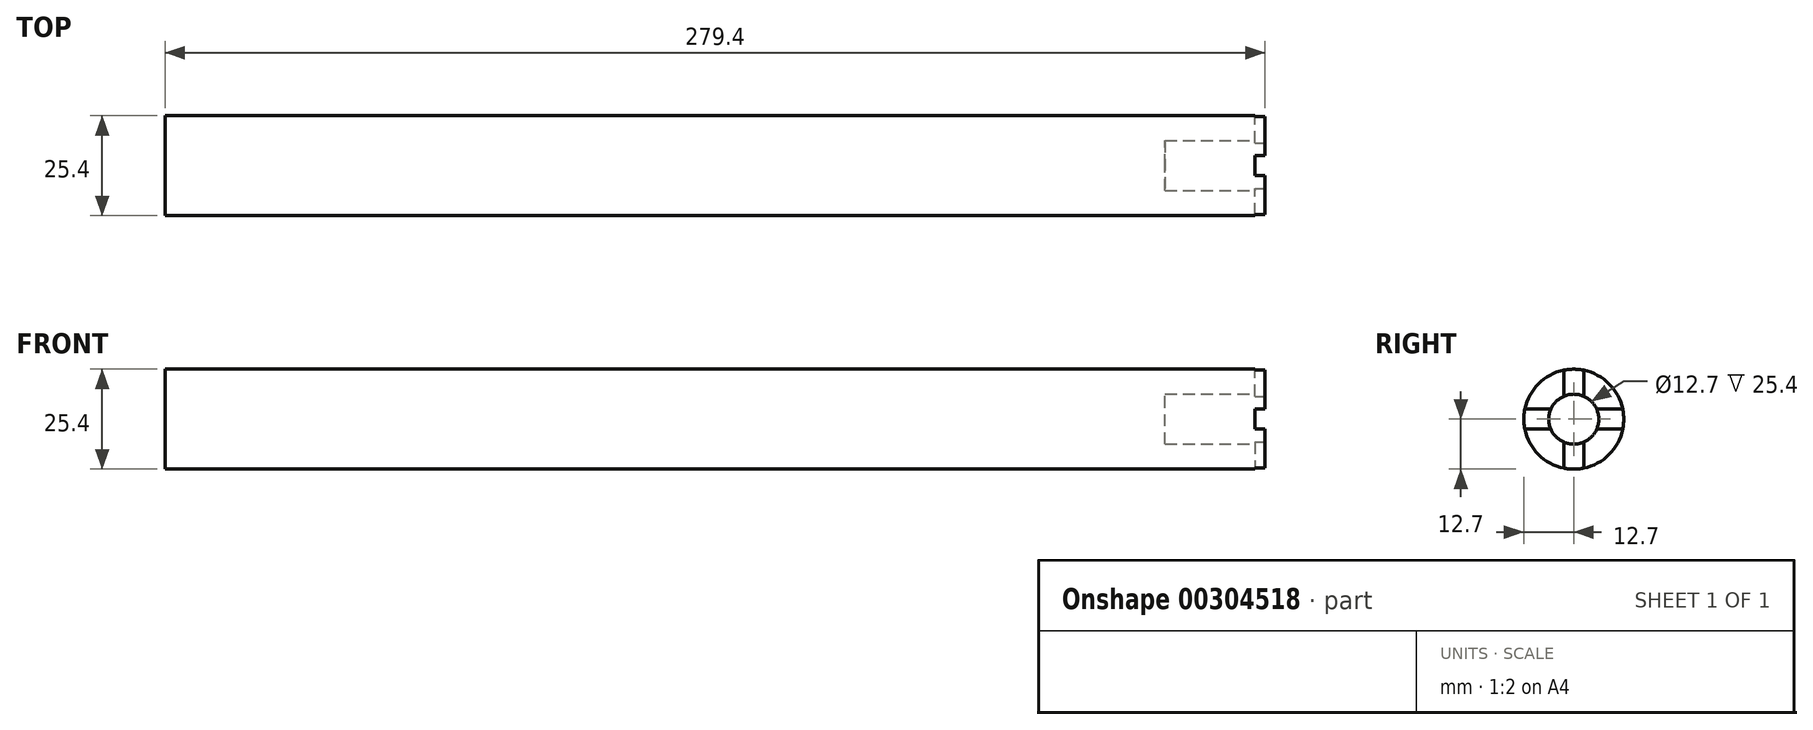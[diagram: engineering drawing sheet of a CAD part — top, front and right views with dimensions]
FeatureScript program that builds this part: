
annotation { "Feature Type Name" : "Feature", "Feature Type Description" : "" }
export const myFeature = defineFeature(function(context is Context, id is Id, definition is map)
    precondition{}
    {
        {
            var Q0;
            Q0=qCreatedBy(makeId("Front.planeOp"),FACE);
            var sketch = newSketch(context, id + "F0", { "sketchPlane" : qUnion([Q0])});
            skLineSegment(sketch, "E0", {"start": v(0, 0) * mm, "end": v(311.8, 0) * mm, "construction": true});
            skLineSegment(sketch, "E1", {"start": v(0, 0) * mm, "end": v(0, 12.7) * mm});
            skLineSegment(sketch, "E2", {"start": v(0, 12.7) * mm, "end": v(279.4, 12.7) * mm});
            skLineSegment(sketch, "E3", {"start": v(279.4, 12.7) * mm, "end": v(279.4, 0) * mm});
            skLineSegment(sketch, "E4", {"start": v(0, 0) * mm, "end": v(66.17, 0) * mm});
            skLineSegment(sketch, "E5", {"start": v(66.17, 0) * mm, "end": v(279.4, 0) * mm});
            skLineSegment(sketch, "E6", {"start": v(260.35, 0) * mm, "end": v(279.4, 0) * mm});
            skLineSegment(sketch, "E7", {"start": v(66.17, 0) * mm, "end": v(66.17, 12.7) * mm});
            skLineSegment(sketch, "E8", {"start": v(260.35, 0) * mm, "end": v(260.35, 12.7) * mm});
            skLineSegment(sketch, "E9", {"start": v(260.35, 12.7) * mm, "end": v(66.17, 12.7) * mm});
            skLineSegment(sketch, "E10", {"start": v(66.17, 0) * mm, "end": v(260.35, 0) * mm});
            skSolve(sketch);
        }
        {
            var Q0;
            Q0 = qSketchRegion(id + "F0", true);
            var Q1;
            Q1=sQuery(id+"F0.wireOp",EDGE,"E0");
            revolve(context, id + "F1", {"entities" : qUnion([Q0]), "axis" : qUnion([Q1]), "revolveType" : RevolveType.FULL});
        }
        {
            var Q0;
            Q0=makeQuery(id+"F1.opRevolve","SWEPT_FACE",FACE,{"disambiguationData":[OSD([sQuery(id+"F0.wireOp",EDGE,"E3")])]});
            var sketch = newSketch(context, id + "F2", { "sketchPlane" : qUnion([Q0])});
            skCircle(sketch, "E11", {"center": v(0, 0) * mm, "radius": 6.35 * mm});
            skLineSegment(sketch, "E12", {"start": v(-12.44, 2.54) * mm, "end": v(-5.82, 2.54) * mm});
            skLineSegment(sketch, "E13", {"start": v(-12.44, -2.54) * mm, "end": v(-5.82, -2.54) * mm});
            skLineSegment(sketch, "E14", {"start": v(-2.54, 5.82) * mm, "end": v(-2.54, 12.44) * mm});
            skLineSegment(sketch, "E15", {"start": v(2.54, 5.82) * mm, "end": v(2.54, 12.44) * mm});
            skLineSegment(sketch, "E16", {"start": v(5.82, 2.54) * mm, "end": v(12.44, 2.54) * mm});
            skLineSegment(sketch, "E17", {"start": v(5.82, -2.54) * mm, "end": v(12.44, -2.54) * mm});
            skLineSegment(sketch, "E18", {"start": v(-2.54, -5.82) * mm, "end": v(-2.54, -12.44) * mm});
            skLineSegment(sketch, "E19", {"start": v(2.54, -5.82) * mm, "end": v(2.54, -12.44) * mm});
            skLineSegment(sketch, "E20", {"start": v(-19.5, 0) * mm, "end": v(23.3, 0) * mm, "construction": true});
            skLineSegment(sketch, "E21", {"start": v(0, 15.45) * mm, "end": v(0, -17.56) * mm, "construction": true});
            skSolve(sketch);
        }
        {
            var Q0;
            {var subQ0=sQuery(id+"F2.wireOp",EDGE,"E14");Q0=makeQuery(id+"F2.imprint","IMPRINT",FACE,{"disambiguationData":[TD([[makeQuery(id+"F2.imprint","IMPRINT",EDGE,{"derivedFrom":subQ0}),-1.0]])]});}
            var Q1;
            {var subQ0=sQuery(id+"F2.wireOp",EDGE,"E12");Q1=makeQuery(id+"F2.imprint","IMPRINT",FACE,{"disambiguationData":[TD([[makeQuery(id+"F2.imprint","IMPRINT",EDGE,{"derivedFrom":subQ0}),-1.0]])]});}
            var Q2;
            {var subQ0=sQuery(id+"F2.wireOp",EDGE,"E18");Q2=makeQuery(id+"F2.imprint","IMPRINT",FACE,{"disambiguationData":[TD([[makeQuery(id+"F2.imprint","IMPRINT",EDGE,{"derivedFrom":subQ0}),1.0]])]});}
            var Q3;
            {var subQ0=sQuery(id+"F2.wireOp",EDGE,"E16");Q3=makeQuery(id+"F2.imprint","IMPRINT",FACE,{"disambiguationData":[TD([[makeQuery(id+"F2.imprint","IMPRINT",EDGE,{"derivedFrom":subQ0}),-1.0]])]});}
            extrude(context, id + "F3", {"entities" : qUnion([Q0, Q1, Q2, Q3]), "operationType" : NewBodyOperationType.REMOVE, "oppositeDirection" : true, "depth" : 2.54 * mm});
        }
        {
            var Q0;
            {var subQ0=sQuery(id+"F2.wireOp",EDGE,"E11");var subQ4=makeQuery(id+"F2.imprint","INTERSECT",VERTEX,{"derivedFrom":[subQ0,sQuery(id+"F2.wireOp",EDGE,"E15")]});Q0=makeQuery(id+"F2.imprint","IMPRINT",FACE,{"disambiguationData":[TD([[makeQuery(id+"F2.imprint","IMPRINT",EDGE,{"disambiguationData":[TD([[subQ4,1.0]])],"derivedFrom":subQ0}),1.0]])]});}
            extrude(context, id + "F4", {"entities" : qUnion([Q0]), "operationType" : NewBodyOperationType.REMOVE, "oppositeDirection" : true, "depth" : 25.4 * mm});
        }
    });
